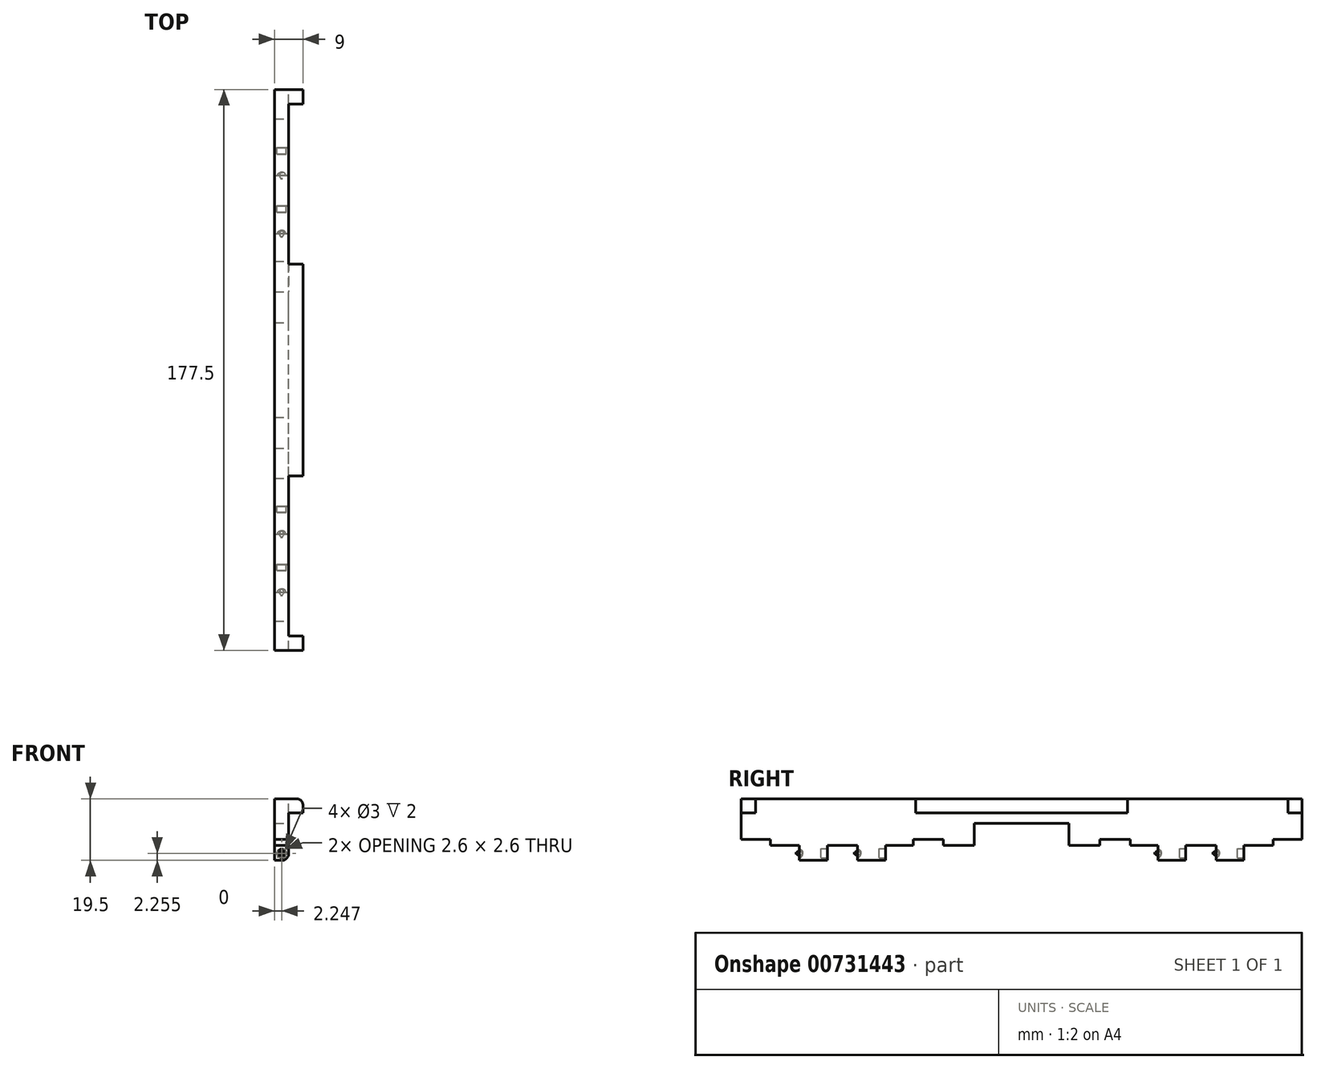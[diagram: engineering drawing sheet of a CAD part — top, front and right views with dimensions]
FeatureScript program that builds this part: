
annotation { "Feature Type Name" : "Feature", "Feature Type Description" : "" }
export const myFeature = defineFeature(function(context is Context, id is Id, definition is map)
    precondition{}
    {
        {
            var Q0;
            Q0=qCreatedBy(makeId("Front.planeOp"),FACE);
            var sketch = newSketch(context, id + "F0", { "sketchPlane" : qUnion([Q0])});
            skLineSegment(sketch, "E0", {"start": v(-4.58, 61.78) * mm, "end": v(-4.58, 66.28) * mm});
            skLineSegment(sketch, "E1", {"start": v(-0.08, -18.72) * mm, "end": v(4.42, -18.72) * mm});
            skLineSegment(sketch, "E2", {"start": v(4.42, -18.72) * mm, "end": v(4.42, -16.22) * mm});
            skLineSegment(sketch, "E3", {"start": v(2.42, -14.22) * mm, "end": v(-4.58, -14.22) * mm});
            skLineSegment(sketch, "E4", {"start": v(-4.58, -33.72) * mm, "end": v(-2.33, -33.72) * mm});
            skLineSegment(sketch, "E5", {"start": v(-0.08, -18.72) * mm, "end": v(-0.08, -31.47) * mm});
            skPoint(sketch, "E6.visualSharp", {"position": v(-0.08, -33.72) * mm});
            skArc(sketch, "E6.filletArc", {"start": v(-2.33, -33.72) * mm, "mid": v(-0.74, -33.06) * mm, "end": v(-0.08, -31.47) * mm});
            skLineSegment(sketch, "E7", {"start": v(-4.58, -31.47) * mm, "end": v(-4.58, -33.72) * mm});
            skLineSegment(sketch, "E8", {"start": v(-4.58, -33.72) * mm, "end": v(-4.58, -14.22) * mm});
            skCircle(sketch, "E9", {"center": v(-2.33, -31.47) * mm, "radius": 1.5 * mm});
            skCircle(sketch, "E10", {"center": v(-2.33, -31.47) * mm, "radius": 1.3 * mm});
            skLineSegment(sketch, "E11", {"start": v(-0.08, -29.02) * mm, "end": v(-4.58, -29.02) * mm});
            skPoint(sketch, "E12.visualSharp", {"position": v(4.42, -14.22) * mm});
            skArc(sketch, "E12.filletArc", {"start": v(4.42, -16.22) * mm, "mid": v(3.83, -14.8) * mm, "end": v(2.42, -14.22) * mm});
            skLineSegment(sketch, "E13", {"start": v(-0.08, -18.72) * mm, "end": v(-0.08, -14.22) * mm});
            skSolve(sketch);
        }
        {
            var Q0;
            {var subQ0=sQuery(id+"F0.wireOp",EDGE,"b09bd09a-8195-43db-865d-672c47637a4f");Q0=makeQuery(id+"F0.imprint","IMPRINT",FACE,{"disambiguationData":[TD([[makeQuery(id+"F0.imprint","IMPRINT",EDGE,{"derivedFrom":subQ0}),-1.0]])]});}
            var Q1;
            {var subQ4=sQuery(id+"F0.wireOp",EDGE,"E4");Q1=makeQuery(id+"F0.imprint","IMPRINT",FACE,{"disambiguationData":[TD([[makeQuery(id+"F0.imprint","IMPRINT",EDGE,{"derivedFrom":subQ4}),1.0]])]});}
            var Q2;
            {var subQ0=sQuery(id+"F0.wireOp",EDGE,"E11");Q2=makeQuery(id+"F0.imprint","IMPRINT",FACE,{"disambiguationData":[TD([[makeQuery(id+"F0.imprint","IMPRINT",EDGE,{"derivedFrom":subQ0}),-1.0]])]});}
            extrude(context, id + "F1", {"entities" : qUnion([Q0, Q1, Q2]), "depth" : 159.1 * mm, "offsetDistance" : 25 * mm});
        }
        {
            var Q0;
            {var subQ1=sQuery(id+"F0.wireOp",EDGE,"E1");Q0=makeQuery(id+"F0.imprint","IMPRINT",FACE,{"disambiguationData":[TD([[makeQuery(id+"F0.imprint","IMPRINT",EDGE,{"derivedFrom":subQ1}),1.0]])]});}
            var Q1;
            {var subQ1=sQuery(id+"F0.wireOp",EDGE,"E4");Q1=makeQuery(id+"F0.imprint","IMPRINT",FACE,{"disambiguationData":[TD([[makeQuery(id+"F0.imprint","IMPRINT",EDGE,{"derivedFrom":subQ1}),1.0]])]});}
            var Q2;
            {var subQ0=sQuery(id+"F0.wireOp",EDGE,"b09bd09a-8195-43db-865d-672c47637a4f");Q2=makeQuery(id+"F0.imprint","IMPRINT",FACE,{"disambiguationData":[TD([[makeQuery(id+"F0.imprint","IMPRINT",EDGE,{"derivedFrom":subQ0}),-1.0]])]});}
            extrude(context, id + "F2", {"entities" : qUnion([Q0, Q1, Q2]), "operationType" : NewBodyOperationType.REMOVE, "depth" : 150.3 * mm, "offsetDistance" : 25 * mm});
        }
        {
            var Q0;
            Q0=makeQuery(id+"F0.imprint","IMPRINT",FACE,{"disambiguationData":[TD([[makeQuery(id+"F0.imprint","IMPRINT",EDGE,{"derivedFrom":sQuery(id+"F0.wireOp",EDGE,"E1")}),1.0]])]});
            var Q1;
            {var subQ0=sQuery(id+"F0.wireOp",EDGE,"E11");Q1=makeQuery(id+"F0.imprint","IMPRINT",FACE,{"disambiguationData":[TD([[makeQuery(id+"F0.imprint","IMPRINT",EDGE,{"derivedFrom":subQ0}),-1.0]])]});}
            extrude(context, id + "F3", {"entities" : qUnion([Q0, Q1]), "operationType" : NewBodyOperationType.ADD, "depth" : 177.5 * mm, "offsetDistance" : 25 * mm});
        }
        {
            var Q0;
            {var subQ0=sQuery(id+"F0.wireOp",EDGE,"b09bd09a-8195-43db-865d-672c47637a4f");Q0=makeQuery(id+"F0.imprint","IMPRINT",FACE,{"disambiguationData":[TD([[makeQuery(id+"F0.imprint","IMPRINT",EDGE,{"derivedFrom":subQ0}),-1.0]])]});}
            var Q1;
            {var subQ4=sQuery(id+"F0.wireOp",EDGE,"E4");Q1=makeQuery(id+"F0.imprint","IMPRINT",FACE,{"disambiguationData":[TD([[makeQuery(id+"F0.imprint","IMPRINT",EDGE,{"derivedFrom":subQ4}),1.0]])]});}
            extrude(context, id + "F4", {"entities" : qUnion([Q0, Q1]), "operationType" : NewBodyOperationType.ADD, "depth" : 140.7 * mm, "offsetDistance" : 25 * mm});
        }
        {
            var Q0;
            {var subQ4=sQuery(id+"F0.wireOp",EDGE,"E4");Q0=makeQuery(id+"F0.imprint","IMPRINT",FACE,{"disambiguationData":[TD([[makeQuery(id+"F0.imprint","IMPRINT",EDGE,{"derivedFrom":subQ4}),1.0]])]});}
            var Q1;
            {var subQ0=sQuery(id+"F0.wireOp",EDGE,"b09bd09a-8195-43db-865d-672c47637a4f");Q1=makeQuery(id+"F0.imprint","IMPRINT",FACE,{"disambiguationData":[TD([[makeQuery(id+"F0.imprint","IMPRINT",EDGE,{"derivedFrom":subQ0}),-1.0]])]});}
            extrude(context, id + "F5", {"entities" : qUnion([Q0, Q1]), "operationType" : NewBodyOperationType.REMOVE, "depth" : 131.9 * mm, "offsetDistance" : 25 * mm});
        }
        {
            var Q0;
            {var subQ0=sQuery(id+"F0.wireOp",EDGE,"b09bd09a-8195-43db-865d-672c47637a4f");Q0=makeQuery(id+"F0.imprint","IMPRINT",FACE,{"disambiguationData":[TD([[makeQuery(id+"F0.imprint","IMPRINT",EDGE,{"derivedFrom":subQ0}),-1.0]])]});}
            var Q1;
            {var subQ4=sQuery(id+"F0.wireOp",EDGE,"E4");Q1=makeQuery(id+"F0.imprint","IMPRINT",FACE,{"disambiguationData":[TD([[makeQuery(id+"F0.imprint","IMPRINT",EDGE,{"derivedFrom":subQ4}),1.0]])]});}
            extrude(context, id + "F6", {"entities" : qUnion([Q0, Q1]), "operationType" : NewBodyOperationType.ADD, "depth" : 45.6 * mm, "offsetDistance" : 25 * mm});
        }
        {
            var Q0;
            {var subQ0=sQuery(id+"F0.wireOp",EDGE,"b09bd09a-8195-43db-865d-672c47637a4f");Q0=makeQuery(id+"F0.imprint","IMPRINT",FACE,{"disambiguationData":[TD([[makeQuery(id+"F0.imprint","IMPRINT",EDGE,{"derivedFrom":subQ0}),-1.0]])]});}
            var Q1;
            {var subQ4=sQuery(id+"F0.wireOp",EDGE,"E4");Q1=makeQuery(id+"F0.imprint","IMPRINT",FACE,{"disambiguationData":[TD([[makeQuery(id+"F0.imprint","IMPRINT",EDGE,{"derivedFrom":subQ4}),1.0]])]});}
            extrude(context, id + "F7", {"entities" : qUnion([Q0, Q1]), "operationType" : NewBodyOperationType.REMOVE, "depth" : 36.8 * mm, "offsetDistance" : 25 * mm});
        }
        {
            var Q0;
            {var subQ0=sQuery(id+"F0.wireOp",EDGE,"b09bd09a-8195-43db-865d-672c47637a4f");Q0=makeQuery(id+"F0.imprint","IMPRINT",FACE,{"disambiguationData":[TD([[makeQuery(id+"F0.imprint","IMPRINT",EDGE,{"derivedFrom":subQ0}),-1.0]])]});}
            var Q1;
            {var subQ4=sQuery(id+"F0.wireOp",EDGE,"E4");Q1=makeQuery(id+"F0.imprint","IMPRINT",FACE,{"disambiguationData":[TD([[makeQuery(id+"F0.imprint","IMPRINT",EDGE,{"derivedFrom":subQ4}),1.0]])]});}
            extrude(context, id + "F8", {"entities" : qUnion([Q0, Q1]), "operationType" : NewBodyOperationType.ADD, "depth" : 27.2 * mm, "offsetDistance" : 25 * mm});
        }
        {
            var Q0;
            {var subQ0=sQuery(id+"F0.wireOp",EDGE,"b09bd09a-8195-43db-865d-672c47637a4f");Q0=makeQuery(id+"F0.imprint","IMPRINT",FACE,{"disambiguationData":[TD([[makeQuery(id+"F0.imprint","IMPRINT",EDGE,{"derivedFrom":subQ0}),-1.0]])]});}
            var Q1;
            {var subQ4=sQuery(id+"F0.wireOp",EDGE,"E4");Q1=makeQuery(id+"F0.imprint","IMPRINT",FACE,{"disambiguationData":[TD([[makeQuery(id+"F0.imprint","IMPRINT",EDGE,{"derivedFrom":subQ4}),1.0]])]});}
            extrude(context, id + "F9", {"entities" : qUnion([Q0, Q1]), "operationType" : NewBodyOperationType.REMOVE, "depth" : 18.4 * mm, "offsetDistance" : 25 * mm});
        }
        {
            var Q0;
            Q0=makeQuery(id+"F0.imprint","IMPRINT",FACE,{"disambiguationData":[TD([[makeQuery(id+"F0.imprint","IMPRINT",EDGE,{"derivedFrom":sQuery(id+"F0.wireOp",EDGE,"E1")}),1.0]])]});
            extrude(context, id + "F10", {"entities" : qUnion([Q0]), "operationType" : NewBodyOperationType.REMOVE, "depth" : 173 * mm, "offsetDistance" : 25 * mm});
        }
        {
            var Q0;
            Q0=makeQuery(id+"F0.imprint","IMPRINT",FACE,{"disambiguationData":[TD([[makeQuery(id+"F0.imprint","IMPRINT",EDGE,{"derivedFrom":sQuery(id+"F0.wireOp",EDGE,"E1")}),1.0]])]});
            extrude(context, id + "F11", {"entities" : qUnion([Q0]), "operationType" : NewBodyOperationType.ADD, "depth" : 122.3 * mm, "offsetDistance" : 25 * mm});
        }
        {
            var Q0;
            Q0=makeQuery(id+"F0.imprint","IMPRINT",FACE,{"disambiguationData":[TD([[makeQuery(id+"F0.imprint","IMPRINT",EDGE,{"derivedFrom":sQuery(id+"F0.wireOp",EDGE,"E1")}),1.0]])]});
            extrude(context, id + "F12", {"entities" : qUnion([Q0]), "operationType" : NewBodyOperationType.REMOVE, "depth" : 55.2 * mm, "offsetDistance" : 25 * mm});
        }
        {
            var Q0;
            Q0=makeQuery(id+"F0.imprint","IMPRINT",FACE,{"disambiguationData":[TD([[makeQuery(id+"F0.imprint","IMPRINT",EDGE,{"derivedFrom":sQuery(id+"F0.wireOp",EDGE,"E1")}),1.0]])]});
            extrude(context, id + "F13", {"entities" : qUnion([Q0]), "operationType" : NewBodyOperationType.ADD, "depth" : 4.5 * mm, "offsetDistance" : 25 * mm});
        }
        {
            var Q0;
            {var subQ0=sQuery(id+"F0.wireOp",EDGE,"E13");var subQ1=sQuery(id+"F0.wireOp",EDGE,"E5");Q0=makeQuery(id+"F12.boolean.opBoolean","MERGE",FACE,{"derivedFrom":[makeQuery(id+"F10.boolean.opBoolean","MERGE",FACE,{"derivedFrom":[makeQuery(id+"F8.boolean.opBoolean","MERGE",FACE,{"derivedFrom":[makeQuery(id+"F6.boolean.opBoolean","MERGE",FACE,{"derivedFrom":[makeQuery(id+"F4.boolean.opBoolean","MERGE",FACE,{"derivedFrom":[makeQuery(id+"F3.boolean.opBoolean","MERGE",FACE,{"derivedFrom":[makeQuery(id+"F1.opExtrude","SWEPT_FACE",FACE,{"disambiguationData":[OSD([subQ1,subQ0])]}),makeQuery(id+"F3.opExtrude","SWEPT_FACE",FACE,{"disambiguationData":[OSD([subQ1])]})]}),makeQuery(id+"F4.opExtrude","SWEPT_FACE",FACE,{"disambiguationData":[OSD([subQ1])]})]}),makeQuery(id+"F6.opExtrude","SWEPT_FACE",FACE,{"disambiguationData":[OSD([subQ1])]})]}),makeQuery(id+"F8.opExtrude","SWEPT_FACE",FACE,{"disambiguationData":[OSD([subQ1])]})]}),makeQuery(id+"F10.opExtrude","SWEPT_FACE",FACE,{"disambiguationData":[OSD([subQ0])]})]}),makeQuery(id+"F12.opExtrude","SWEPT_FACE",FACE,{"disambiguationData":[OSD([subQ0])]})]});}
            var sketch = newSketch(context, id + "F14", { "sketchPlane" : qUnion([Q0])});
            skLineSegment(sketch, "E14.bottom", {"start": v(-103.75, -29.02) * mm, "end": v(-73.75, -29.02) * mm});
            skLineSegment(sketch, "E14.top", {"start": v(-103.75, -22.02) * mm, "end": v(-73.75, -22.02) * mm});
            skLineSegment(sketch, "E14.left", {"start": v(-103.75, -29.02) * mm, "end": v(-103.75, -22.02) * mm});
            skLineSegment(sketch, "E14.right", {"start": v(-73.75, -29.02) * mm, "end": v(-73.75, -22.02) * mm});
            skLineSegment(sketch, "E15.bottom", {"start": v(0, -29.02) * mm, "end": v(-9.2, -29.02) * mm});
            skLineSegment(sketch, "E15.top", {"start": v(0, -27.02) * mm, "end": v(-9.2, -27.02) * mm});
            skLineSegment(sketch, "E15.left", {"start": v(0, -29.02) * mm, "end": v(0, -27.02) * mm});
            skLineSegment(sketch, "E15.right", {"start": v(-9.2, -29.02) * mm, "end": v(-9.2, -27.02) * mm});
            skLineSegment(sketch, "E16.bottom", {"start": v(-54.4, -29.02) * mm, "end": v(-64, -29.02) * mm});
            skLineSegment(sketch, "E16.top", {"start": v(-54.4, -27.02) * mm, "end": v(-64, -27.02) * mm});
            skLineSegment(sketch, "E16.left", {"start": v(-54.4, -29.02) * mm, "end": v(-54.4, -27.02) * mm});
            skLineSegment(sketch, "E16.right", {"start": v(-64, -29.02) * mm, "end": v(-64, -27.02) * mm});
            skPoint(sketch, "E17.oppositeSnap0", {"position": v(-59.2, -27.02) * mm});
            skLineSegment(sketch, "E17.bottom", {"start": v(-123.1, -29.02) * mm, "end": v(-113.5, -29.02) * mm});
            skLineSegment(sketch, "E17.top", {"start": v(-123.1, -27.02) * mm, "end": v(-113.5, -27.02) * mm});
            skLineSegment(sketch, "E17.left", {"start": v(-123.1, -29.02) * mm, "end": v(-123.1, -27.02) * mm});
            skLineSegment(sketch, "E17.right", {"start": v(-113.5, -29.02) * mm, "end": v(-113.5, -27.02) * mm});
            skLineSegment(sketch, "E18.bottom", {"start": v(-168.3, -29.02) * mm, "end": v(-177.5, -29.02) * mm});
            skLineSegment(sketch, "E18.top", {"start": v(-168.3, -27.02) * mm, "end": v(-177.5, -27.02) * mm});
            skLineSegment(sketch, "E18.left", {"start": v(-168.3, -29.02) * mm, "end": v(-168.3, -27.02) * mm});
            skLineSegment(sketch, "E18.right", {"start": v(-177.5, -29.02) * mm, "end": v(-177.5, -27.02) * mm});
            skSolve(sketch);
        }
        {
            var Q0;
            Q0=makeQuery(id+"F14.imprint","IMPRINT",FACE,{"disambiguationData":[TD([[makeQuery(id+"F14.imprint","IMPRINT",EDGE,{"derivedFrom":sQuery(id+"F14.wireOp",EDGE,"E14.bottom")}),1.0]])]});
            var Q1;
            Q1=makeQuery(id+"F14.imprint","IMPRINT",FACE,{"disambiguationData":[TD([[makeQuery(id+"F14.imprint","IMPRINT",EDGE,{"derivedFrom":sQuery(id+"F14.wireOp",EDGE,"E16.bottom")}),1.0]])]});
            var Q2;
            Q2=makeQuery(id+"F14.imprint","IMPRINT",FACE,{"disambiguationData":[TD([[makeQuery(id+"F14.imprint","IMPRINT",EDGE,{"derivedFrom":sQuery(id+"F14.wireOp",EDGE,"E15.bottom")}),1.0]])]});
            var Q3;
            Q3=makeQuery(id+"F14.imprint","IMPRINT",FACE,{"disambiguationData":[TD([[makeQuery(id+"F14.imprint","IMPRINT",EDGE,{"derivedFrom":sQuery(id+"F14.wireOp",EDGE,"E17.bottom")}),1.0]])]});
            var Q4;
            Q4=makeQuery(id+"F14.imprint","IMPRINT",FACE,{"disambiguationData":[TD([[makeQuery(id+"F14.imprint","IMPRINT",EDGE,{"derivedFrom":sQuery(id+"F14.wireOp",EDGE,"E18.bottom")}),1.0]])]});
            extrude(context, id + "F15", {"entities" : qUnion([Q0, Q1, Q2, Q3, Q4]), "operationType" : NewBodyOperationType.REMOVE, "oppositeDirection" : true, "depth" : 25 * mm, "offsetDistance" : 25 * mm});
        }
        {
            var Q0;
            Q0=makeQuery(id+"F9.boolean.opBoolean","COPY",FACE,{"derivedFrom":makeQuery(id+"F9.opExtrude","CAP_FACE",FACE,{"disambiguationData":[OSD([sQuery(id+"F0.wireOp",EDGE,"E4"),sQuery(id+"F0.wireOp",EDGE,"E5"),sQuery(id+"F0.wireOp",EDGE,"E6.filletArc"),sQuery(id+"F0.wireOp",EDGE,"E8"),sQuery(id+"F0.wireOp",EDGE,"E9"),sQuery(id+"F0.wireOp",EDGE,"E11")])],"isStart":false})});
            var sketch = newSketch(context, id + "F16", { "sketchPlane" : qUnion([Q0])});
            skCircle(sketch, "E19", {"center": v(2.33, -31.47) * mm, "radius": 1.3 * mm});
            skCircle(sketch, "E20", {"center": v(2.33, -31.47) * mm, "radius": 1.5 * mm});
            skSolve(sketch);
        }
        {
            var Q0;
            Q0=makeQuery(id+"F7.boolean.opBoolean","COPY",FACE,{"derivedFrom":makeQuery(id+"F7.opExtrude","CAP_FACE",FACE,{"disambiguationData":[OSD([sQuery(id+"F0.wireOp",EDGE,"E4"),sQuery(id+"F0.wireOp",EDGE,"E5"),sQuery(id+"F0.wireOp",EDGE,"E6.filletArc"),sQuery(id+"F0.wireOp",EDGE,"E8"),sQuery(id+"F0.wireOp",EDGE,"E9"),sQuery(id+"F0.wireOp",EDGE,"E11")])],"isStart":false})});
            var sketch = newSketch(context, id + "F17", { "sketchPlane" : qUnion([Q0])});
            skCircle(sketch, "E21", {"center": v(2.33, -31.47) * mm, "radius": 1.3 * mm});
            skCircle(sketch, "E22", {"center": v(2.33, -31.47) * mm, "radius": 1.5 * mm});
            skSolve(sketch);
        }
        {
            var Q0;
            Q0=makeQuery(id+"F5.boolean.opBoolean","COPY",FACE,{"derivedFrom":makeQuery(id+"F5.opExtrude","CAP_FACE",FACE,{"disambiguationData":[OSD([sQuery(id+"F0.wireOp",EDGE,"E4"),sQuery(id+"F0.wireOp",EDGE,"E5"),sQuery(id+"F0.wireOp",EDGE,"E6.filletArc"),sQuery(id+"F0.wireOp",EDGE,"E8"),sQuery(id+"F0.wireOp",EDGE,"E9"),sQuery(id+"F0.wireOp",EDGE,"E11")])],"isStart":false})});
            var sketch = newSketch(context, id + "F18", { "sketchPlane" : qUnion([Q0])});
            skCircle(sketch, "E23", {"center": v(2.33, -31.47) * mm, "radius": 1.3 * mm});
            skCircle(sketch, "E24", {"center": v(2.33, -31.47) * mm, "radius": 1.5 * mm});
            skSolve(sketch);
        }
        {
            var Q0;
            Q0=makeQuery(id+"F2.boolean.opBoolean","COPY",FACE,{"derivedFrom":makeQuery(id+"F2.opExtrude","CAP_FACE",FACE,{"disambiguationData":[OSD([sQuery(id+"F0.wireOp",EDGE,"E4"),sQuery(id+"F0.wireOp",EDGE,"E5"),sQuery(id+"F0.wireOp",EDGE,"E6.filletArc"),sQuery(id+"F0.wireOp",EDGE,"E8"),sQuery(id+"F0.wireOp",EDGE,"E9"),sQuery(id+"F0.wireOp",EDGE,"E11")])],"isStart":false})});
            var sketch = newSketch(context, id + "F19", { "sketchPlane" : qUnion([Q0])});
            skCircle(sketch, "E25", {"center": v(2.33, -31.47) * mm, "radius": 1.3 * mm});
            skCircle(sketch, "E26", {"center": v(2.33, -31.47) * mm, "radius": 1.5 * mm});
            skSolve(sketch);
        }
        {
            var Q0;
            Q0=makeQuery(id+"F16.imprint","IMPRINT",FACE,{"disambiguationData":[TD([[makeQuery(id+"F16.imprint","IMPRINT",EDGE,{"derivedFrom":sQuery(id+"F16.wireOp",EDGE,"E19")}),-1.0]])]});
            var Q1;
            Q1=makeQuery(id+"F17.imprint","IMPRINT",FACE,{"disambiguationData":[TD([[makeQuery(id+"F17.imprint","IMPRINT",EDGE,{"derivedFrom":sQuery(id+"F17.wireOp",EDGE,"E21")}),-1.0]])]});
            var Q2;
            Q2=makeQuery(id+"F18.imprint","IMPRINT",FACE,{"disambiguationData":[TD([[makeQuery(id+"F18.imprint","IMPRINT",EDGE,{"derivedFrom":sQuery(id+"F18.wireOp",EDGE,"E23")}),-1.0]])]});
            var Q3;
            Q3=makeQuery(id+"F19.imprint","IMPRINT",FACE,{"disambiguationData":[TD([[makeQuery(id+"F19.imprint","IMPRINT",EDGE,{"derivedFrom":sQuery(id+"F19.wireOp",EDGE,"E25")}),-1.0]])]});
            extrude(context, id + "F20", {"entities" : qUnion([Q0, Q1, Q2, Q3]), "operationType" : NewBodyOperationType.ADD, "oppositeDirection" : true, "depth" : 8.8 * mm, "offsetDistance" : 25 * mm});
        }
        {
            var Q0;
            Q0=makeQuery(id+"F16.imprint","IMPRINT",FACE,{"disambiguationData":[TD([[makeQuery(id+"F16.imprint","IMPRINT",EDGE,{"derivedFrom":sQuery(id+"F16.wireOp",EDGE,"E19")}),1.0]])]});
            var Q1;
            Q1=makeQuery(id+"F17.imprint","IMPRINT",FACE,{"disambiguationData":[TD([[makeQuery(id+"F17.imprint","IMPRINT",EDGE,{"derivedFrom":sQuery(id+"F17.wireOp",EDGE,"E21")}),1.0]])]});
            var Q2;
            Q2=makeQuery(id+"F18.imprint","IMPRINT",FACE,{"disambiguationData":[TD([[makeQuery(id+"F18.imprint","IMPRINT",EDGE,{"derivedFrom":sQuery(id+"F18.wireOp",EDGE,"E23")}),1.0]])]});
            var Q3;
            Q3=makeQuery(id+"F19.imprint","IMPRINT",FACE,{"disambiguationData":[TD([[makeQuery(id+"F19.imprint","IMPRINT",EDGE,{"derivedFrom":sQuery(id+"F19.wireOp",EDGE,"E25")}),1.0]])]});
            extrude(context, id + "F21", {"entities" : qUnion([Q0, Q1, Q2, Q3]), "operationType" : NewBodyOperationType.ADD, "oppositeDirection" : true, "depth" : 9.8 * mm, "offsetDistance" : 25 * mm});
        }
        {
            var Q0;
            Q0=makeQuery(id+"F16.imprint","IMPRINT",FACE,{"disambiguationData":[TD([[makeQuery(id+"F16.imprint","IMPRINT",EDGE,{"derivedFrom":sQuery(id+"F16.wireOp",EDGE,"E19")}),1.0]])]});
            var Q1;
            Q1=makeQuery(id+"F16.imprint","IMPRINT",FACE,{"disambiguationData":[TD([[makeQuery(id+"F16.imprint","IMPRINT",EDGE,{"derivedFrom":sQuery(id+"F16.wireOp",EDGE,"E19")}),-1.0]])]});
            var Q2;
            Q2=makeQuery(id+"F17.imprint","IMPRINT",FACE,{"disambiguationData":[TD([[makeQuery(id+"F17.imprint","IMPRINT",EDGE,{"derivedFrom":sQuery(id+"F17.wireOp",EDGE,"E21")}),-1.0]])]});
            var Q3;
            Q3=makeQuery(id+"F17.imprint","IMPRINT",FACE,{"disambiguationData":[TD([[makeQuery(id+"F17.imprint","IMPRINT",EDGE,{"derivedFrom":sQuery(id+"F17.wireOp",EDGE,"E21")}),1.0]])]});
            var Q4;
            Q4=makeQuery(id+"F18.imprint","IMPRINT",FACE,{"disambiguationData":[TD([[makeQuery(id+"F18.imprint","IMPRINT",EDGE,{"derivedFrom":sQuery(id+"F18.wireOp",EDGE,"E23")}),1.0]])]});
            var Q5;
            Q5=makeQuery(id+"F18.imprint","IMPRINT",FACE,{"disambiguationData":[TD([[makeQuery(id+"F18.imprint","IMPRINT",EDGE,{"derivedFrom":sQuery(id+"F18.wireOp",EDGE,"E23")}),-1.0]])]});
            var Q6;
            Q6=makeQuery(id+"F19.imprint","IMPRINT",FACE,{"disambiguationData":[TD([[makeQuery(id+"F19.imprint","IMPRINT",EDGE,{"derivedFrom":sQuery(id+"F19.wireOp",EDGE,"E25")}),1.0]])]});
            var Q7;
            Q7=makeQuery(id+"F19.imprint","IMPRINT",FACE,{"disambiguationData":[TD([[makeQuery(id+"F19.imprint","IMPRINT",EDGE,{"derivedFrom":sQuery(id+"F19.wireOp",EDGE,"E25")}),-1.0]])]});
            extrude(context, id + "F22", {"entities" : qUnion([Q0, Q1, Q2, Q3, Q4, Q5, Q6, Q7]), "operationType" : NewBodyOperationType.REMOVE, "oppositeDirection" : true, "depth" : 2 * mm, "offsetDistance" : 25 * mm});
        }
        {
            var Q0;
            Q0=makeQuery(id+"F21.opExtrude","CAP_EDGE",EDGE,{"disambiguationData":[OSD([sQuery(id+"F16.wireOp",EDGE,"E19")])],"isStart":false});
            var Q1;
            Q1=makeQuery(id+"F21.opExtrude","CAP_EDGE",EDGE,{"disambiguationData":[OSD([sQuery(id+"F17.wireOp",EDGE,"E21")])],"isStart":false});
            var Q2;
            Q2=makeQuery(id+"F21.opExtrude","CAP_EDGE",EDGE,{"disambiguationData":[OSD([sQuery(id+"F18.wireOp",EDGE,"E23")])],"isStart":false});
            var Q3;
            Q3=makeQuery(id+"F21.opExtrude","CAP_EDGE",EDGE,{"disambiguationData":[OSD([sQuery(id+"F19.wireOp",EDGE,"E25")])],"isStart":false});
            fillet(context, id + "F23", {"entities" : qUnion([Q0, Q1, Q2, Q3]), "radius" : 1 * mm, "tangentPropagation" : true, "allowEdgeOverflow" : false});
        }
    });
